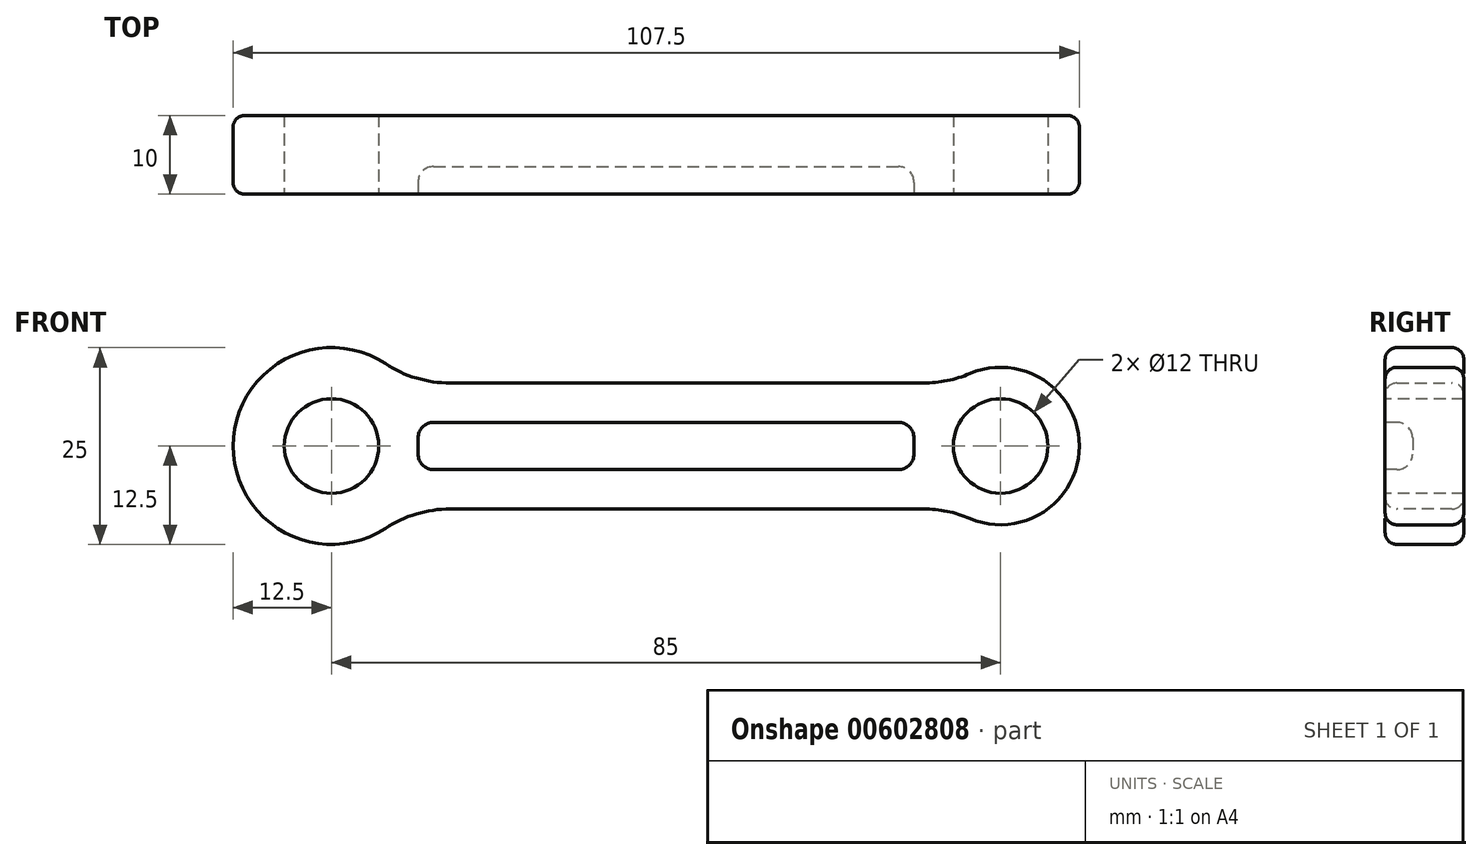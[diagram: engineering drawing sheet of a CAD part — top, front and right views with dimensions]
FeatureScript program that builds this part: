
annotation { "Feature Type Name" : "Feature", "Feature Type Description" : "" }
export const myFeature = defineFeature(function(context is Context, id is Id, definition is map)
    precondition{}
    {
        {
            var Q0;
            Q0=qCreatedBy(makeId("Front.planeOp"),FACE);
            var sketch = newSketch(context, id + "F0", { "sketchPlane" : qUnion([Q0])});
            skCircle(sketch, "E0", {"center": v(0, 0) * mm, "radius": 12.5 * mm});
            skCircle(sketch, "E1", {"center": v(85, 0) * mm, "radius": 10 * mm});
            skLineSegment(sketch, "E2", {"start": v(0, 0) * mm, "end": v(85, 0) * mm, "construction": true});
            skLineSegment(sketch, "E3", {"start": v(9.6, 8) * mm, "end": v(79, 8) * mm});
            skLineSegment(sketch, "E4.MirrorCS", {"start": v(9.6, -8) * mm, "end": v(79, -8) * mm});
            skSolve(sketch);
        }
        {
            var Q0;
            {var subQ0=sQuery(id+"F0.wireOp",EDGE,"E0");var subQ1=makeQuery(id+"F0.imprint","INTERSECT",VERTEX,{"derivedFrom":[subQ0,sQuery(id+"F0.wireOp",EDGE,"E3")]});Q0=makeQuery(id+"F0.imprint","IMPRINT",FACE,{"disambiguationData":[TD([[makeQuery(id+"F0.imprint","IMPRINT",EDGE,{"disambiguationData":[TD([[subQ1,-1.0]])],"derivedFrom":subQ0}),1.0]])]});}
            var Q1;
            {var subQ0=sQuery(id+"F0.wireOp",EDGE,"E3");Q1=makeQuery(id+"F0.imprint","IMPRINT",FACE,{"disambiguationData":[TD([[makeQuery(id+"F0.imprint","IMPRINT",EDGE,{"derivedFrom":subQ0}),-1.0]])]});}
            var Q2;
            {var subQ0=sQuery(id+"F0.wireOp",EDGE,"E1");var subQ1=makeQuery(id+"F0.imprint","INTERSECT",VERTEX,{"derivedFrom":[subQ0,sQuery(id+"F0.wireOp",EDGE,"E3")]});Q2=makeQuery(id+"F0.imprint","IMPRINT",FACE,{"disambiguationData":[TD([[makeQuery(id+"F0.imprint","IMPRINT",EDGE,{"disambiguationData":[TD([[subQ1,-1.0]])],"derivedFrom":subQ0}),1.0]])]});}
            extrude(context, id + "F1", {"entities" : qUnion([Q0, Q1, Q2]), "depth" : 10 * mm, "offsetDistance" : 25 * mm, "symmetric" : true});
        }
        {
            var Q0;
            Q0=makeQuery(id+"F1.opExtrude","CAP_FACE",FACE,{"disambiguationData":[OSD([sQuery(id+"F0.wireOp",EDGE,"E0"),sQuery(id+"F0.wireOp",EDGE,"E1"),sQuery(id+"F0.wireOp",EDGE,"E3"),sQuery(id+"F0.wireOp",EDGE,"E4.MirrorCS")])],"isStart":false});
            var sketch = newSketch(context, id + "F2", { "sketchPlane" : qUnion([Q0])});
            skPoint(sketch, "E5", {"position": v(0, 0) * mm});
            skPoint(sketch, "E6", {"position": v(85, 0) * mm});
            skSolve(sketch);
        }
        {
            var Q0;
            Q0=sQuery(id+"F2.wireOp",VERTEX,"E6");
            var Q1;
            Q1=sQuery(id+"F2.wireOp",VERTEX,"E5");
            var Q2;
            Q2=makeQuery(id+"F1.opExtrude","SWEPT_BODY",BODY,{"disambiguationData":[OSD([sQuery(id+"F0.wireOp",EDGE,"E0"),sQuery(id+"F0.wireOp",EDGE,"E1"),sQuery(id+"F0.wireOp",EDGE,"E3"),sQuery(id+"F0.wireOp",EDGE,"E4.MirrorCS")])]});
            hole(context, id + "F3", {"style" : HoleStyle.SIMPLE, "endStyle" : HoleEndStyle.THROUGH, "standardTappedOrClearance" : lookupTablePath({ "standard" : "ISO", "size" : "12", "type" : "Drilled" }), "standardBlindInLast" : lookupTablePath({ "standard" : "ISO", "size" : "12", "type" : "Drilled" }), "holeDiameter" : 12 * mm, "majorDiameter" : 12 * mm, "isTappedThrough" : true, "tappedDepth" : 12 * mm, "tapClearance" : 3, "locations" : qUnion([Q0, Q1]), "scope" : qUnion([Q2])});
        }
        {
            var Q0;
            Q0=makeQuery(id+"F1.opExtrude","SWEPT_EDGE",EDGE,{"disambiguationData":[OSD([sQuery(id+"F0.wireOp",EDGE,"E0"),sQuery(id+"F0.wireOp",EDGE,"E3")])]});
            var Q1;
            Q1=makeQuery(id+"F1.opExtrude","SWEPT_EDGE",EDGE,{"disambiguationData":[OSD([sQuery(id+"F0.wireOp",EDGE,"E0"),sQuery(id+"F0.wireOp",EDGE,"E4.MirrorCS")])]});
            var Q2;
            Q2=makeQuery(id+"F1.opExtrude","SWEPT_EDGE",EDGE,{"disambiguationData":[OSD([sQuery(id+"F0.wireOp",EDGE,"E1"),sQuery(id+"F0.wireOp",EDGE,"E3")])]});
            var Q3;
            Q3=makeQuery(id+"F1.opExtrude","SWEPT_EDGE",EDGE,{"disambiguationData":[OSD([sQuery(id+"F0.wireOp",EDGE,"E1"),sQuery(id+"F0.wireOp",EDGE,"E4.MirrorCS")])]});
            fillet(context, id + "F4", {"entities" : qUnion([Q0, Q1, Q2, Q3]), "radius" : 15 * mm, "tangentPropagation" : true, "allowEdgeOverflow" : false});
        }
        {
            var Q0;
            Q0=makeQuery(id+"F1.opExtrude","CAP_FACE",FACE,{"disambiguationData":[OSD([sQuery(id+"F0.wireOp",EDGE,"E0"),sQuery(id+"F0.wireOp",EDGE,"E1"),sQuery(id+"F0.wireOp",EDGE,"E3"),sQuery(id+"F0.wireOp",EDGE,"E4.MirrorCS")])],"isStart":false});
            var sketch = newSketch(context, id + "F5", { "sketchPlane" : qUnion([Q0])});
            skLineSegment(sketch, "E7.bottom", {"start": v(11, 3) * mm, "end": v(74, 3) * mm});
            skLineSegment(sketch, "E7.top", {"start": v(11, -3) * mm, "end": v(74, -3) * mm});
            skLineSegment(sketch, "E7.left", {"start": v(11, 3) * mm, "end": v(11, -3) * mm});
            skLineSegment(sketch, "E7.right", {"start": v(74, 3) * mm, "end": v(74, -3) * mm});
            skSolve(sketch);
        }
        {
            var Q0;
            Q0=makeQuery(id+"F5.imprint","IMPRINT",FACE,{"disambiguationData":[TD([[makeQuery(id+"F5.imprint","IMPRINT",EDGE,{"derivedFrom":sQuery(id+"F5.wireOp",EDGE,"E7.bottom")}),-1.0]])]});
            extrude(context, id + "F6", {"entities" : qUnion([Q0]), "operationType" : NewBodyOperationType.REMOVE, "oppositeDirection" : true, "depth" : 3.5 * mm, "offsetDistance" : 25 * mm});
        }
        {
            var Q0;
            Q0=makeQuery(id+"F6.boolean.opBoolean","COPY",EDGE,{"derivedFrom":makeQuery(id+"F6.opExtrude","CAP_EDGE",EDGE,{"disambiguationData":[OSD([sQuery(id+"F5.wireOp",EDGE,"E7.top")])],"isStart":false})});
            var Q1;
            Q1=makeQuery(id+"F6.boolean.opBoolean","COPY",FACE,{"derivedFrom":makeQuery(id+"F6.opExtrude","CAP_FACE",FACE,{"disambiguationData":[OSD([sQuery(id+"F5.wireOp",EDGE,"E7.bottom"),sQuery(id+"F5.wireOp",EDGE,"E7.top"),sQuery(id+"F5.wireOp",EDGE,"E7.left"),sQuery(id+"F5.wireOp",EDGE,"E7.right")])],"isStart":false})});
            var Q2;
            Q2=makeQuery(id+"F6.boolean.opBoolean","COPY",EDGE,{"derivedFrom":makeQuery(id+"F6.opExtrude","SWEPT_EDGE",EDGE,{"disambiguationData":[OSD([sQuery(id+"F5.wireOp",EDGE,"E7.top"),sQuery(id+"F5.wireOp",EDGE,"E7.left")])]})});
            var Q3;
            Q3=makeQuery(id+"F6.boolean.opBoolean","COPY",EDGE,{"derivedFrom":makeQuery(id+"F6.opExtrude","SWEPT_EDGE",EDGE,{"disambiguationData":[OSD([sQuery(id+"F5.wireOp",EDGE,"E7.bottom"),sQuery(id+"F5.wireOp",EDGE,"E7.left")])]})});
            var Q4;
            Q4=makeQuery(id+"F6.boolean.opBoolean","COPY",EDGE,{"derivedFrom":makeQuery(id+"F6.opExtrude","SWEPT_EDGE",EDGE,{"disambiguationData":[OSD([sQuery(id+"F5.wireOp",EDGE,"E7.bottom"),sQuery(id+"F5.wireOp",EDGE,"E7.right")])]})});
            var Q5;
            Q5=makeQuery(id+"F6.boolean.opBoolean","COPY",EDGE,{"derivedFrom":makeQuery(id+"F6.opExtrude","SWEPT_EDGE",EDGE,{"disambiguationData":[OSD([sQuery(id+"F5.wireOp",EDGE,"E7.top"),sQuery(id+"F5.wireOp",EDGE,"E7.right")])]})});
            fillet(context, id + "F7", {"entities" : qUnion([Q0, Q1, Q2, Q3, Q4, Q5]), "radius" : 2 * mm, "tangentPropagation" : true, "allowEdgeOverflow" : false});
        }
        {
            var Q0;
            Q0=makeQuery(id+"F1.opExtrude","CAP_EDGE",EDGE,{"disambiguationData":[OSD([sQuery(id+"F0.wireOp",EDGE,"E0")])],"isStart":false});
            var Q1;
            {var subQ0=sQuery(id+"F0.wireOp",EDGE,"E3");var subQ1=sQuery(id+"F0.wireOp",EDGE,"E0");Q1=makeQuery(id+"F4.opFillet","BLEND_EDGE",EDGE,{"blendedFrom":[makeQuery(id+"F1.opExtrude","SWEPT_EDGE",EDGE,{"disambiguationData":[OSD([subQ1,subQ0])]}),makeQuery(id+"F1.opExtrude","CAP_FACE",FACE,{"disambiguationData":[OSD([subQ1,sQuery(id+"F0.wireOp",EDGE,"E1"),subQ0,sQuery(id+"F0.wireOp",EDGE,"E4.MirrorCS")])],"isStart":false})],"blendedInto":[makeQuery(id+"F1.opExtrude","CAP_FACE",FACE,{"disambiguationData":[OSD([subQ1,sQuery(id+"F0.wireOp",EDGE,"E1"),subQ0,sQuery(id+"F0.wireOp",EDGE,"E4.MirrorCS")])],"isStart":false})]});}
            var Q2;
            Q2=makeQuery(id+"F1.opExtrude","CAP_EDGE",EDGE,{"disambiguationData":[OSD([sQuery(id+"F0.wireOp",EDGE,"E1")])],"isStart":true});
            fillet(context, id + "F8", {"entities" : qUnion([Q0, Q1, Q2]), "radius" : 1.5 * mm, "tangentPropagation" : true, "allowEdgeOverflow" : false});
        }
    });
